# Revit family: Storage-Teknion-CWRS_Teknion_Reception_Console-R2016
name_source: partatom
category: Furniture
revit_build: Autodesk Revit 2018 (Build: 20190510_1515(x64)
units: mm (PartAtom-declared; Revit-internal decimal feet)

## family parameters
Always vertical = Yes
Cut with Voids When Loaded = No
OmniClass Number = 23.40.20.00
OmniClass Title = General Furniture and Specialties
Room Calculation Point = No
Shared = Yes
Work Plane-Based = No

## types (3) — shared parameters
Assembly Code = E2020200
Manufacturer = Teknion
Manufacturer Fax = 416.661.4586
Part Number = CWRS
Product Documentation Link = https://assets.teknion.com
Product Line = Teknion Reception
Product Page URL = https://www.teknion.com
Series = Custom Wood
Sustainability Data = https://www.teknion.com
URL = www.teknion.com
Unit Weight URL = http://www.teknion.com
Warranty = http://www.teknion.com

## per-type parameters (varying)
| type | 2N | 3N | 4T | Bottom Trim Offset | Description | Height | Model | Not 2N | Not 4T | Side Top Offsets |
| 29" Height, No Top Divider | Yes | No | No | 1.02 " | Teknion Reception, Console Storage, 29" Height, No Top Divider | 29 " | CWRS2N_______ | No | Yes | 27.961 " |
| 36" Height, No Top Divider | No | Yes | No | 2.343 " | Teknion Reception, Console Storage, 36" Height, No Top Divider | 36 " | CWRS3N_______ | Yes | Yes | 34.961 " |
| 40" Height, 36" H Storage with Top Divider | No | No | Yes | 2.343 " | Teknion Reception, Console Storage, 40" Height, 36" H Storage with Top Divider | 42 " | CWRS4T_______ | Yes | No | 42 " |

## geometry (parser evidence)
native form markers: Blend x32, Sweep x3
no freeform markers — native parametric forms only
